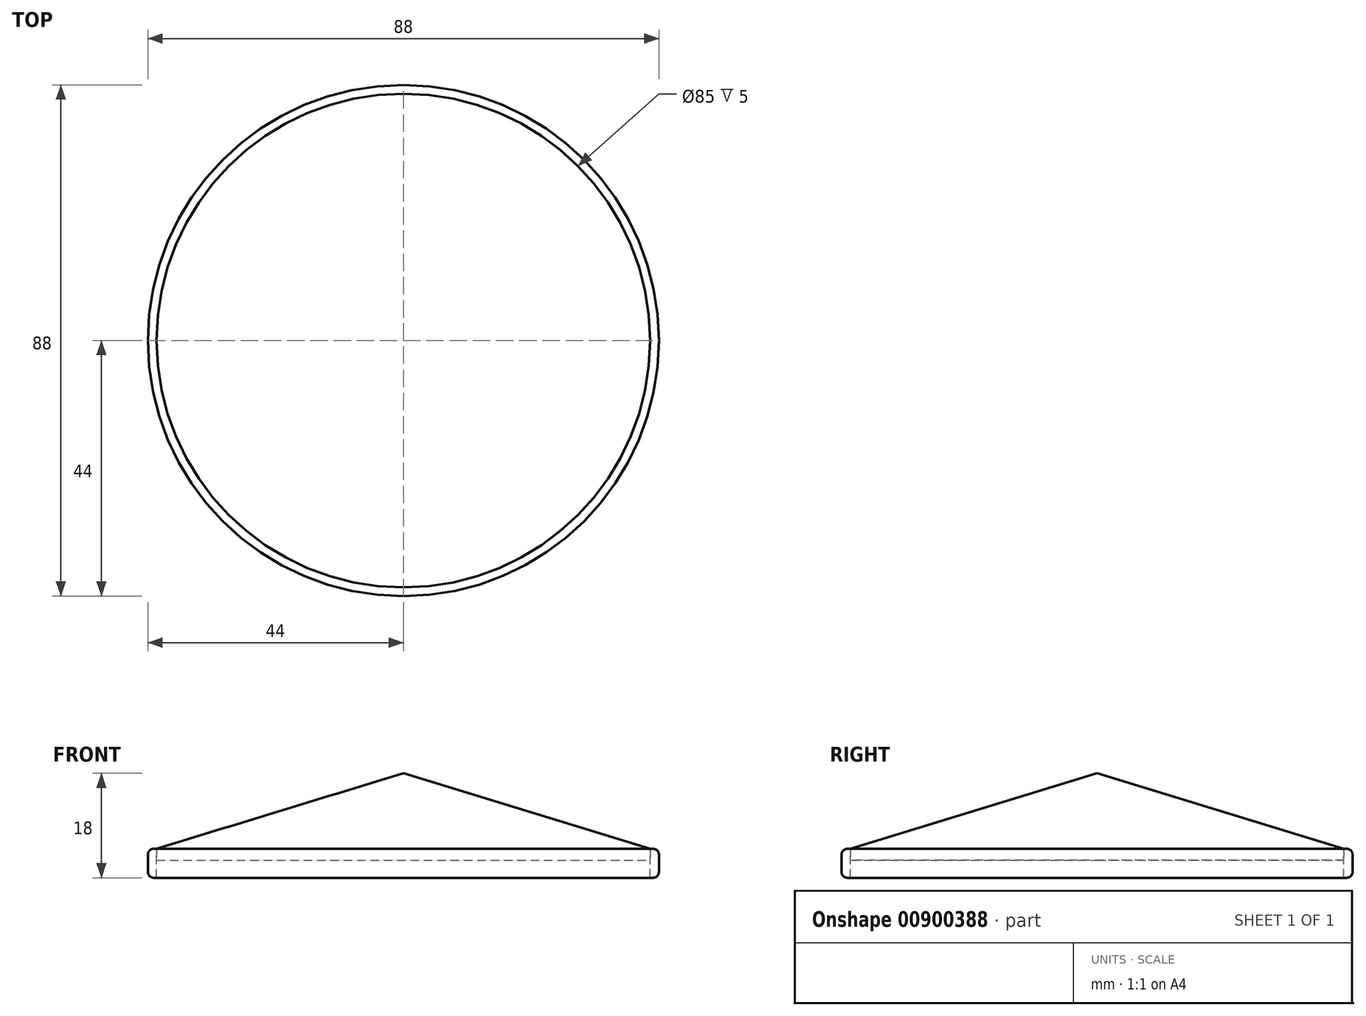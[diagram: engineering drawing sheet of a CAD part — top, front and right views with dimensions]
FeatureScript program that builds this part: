
annotation { "Feature Type Name" : "Feature", "Feature Type Description" : "" }
export const myFeature = defineFeature(function(context is Context, id is Id, definition is map)
    precondition{}
    {
        {
            var Q0;
            Q0=qCreatedBy(makeId("Front.planeOp"),FACE);
            var sketch = newSketch(context, id + "F0", { "sketchPlane" : qUnion([Q0])});
            skLineSegment(sketch, "E0", {"start": v(0, 0) * mm, "end": v(0, 15) * mm});
            skLineSegment(sketch, "E1", {"start": v(42.5, 0) * mm, "end": v(0, 0) * mm});
            skLineSegment(sketch, "E2", {"start": v(42.5, 0) * mm, "end": v(42.5, 2) * mm});
            skLineSegment(sketch, "E3", {"start": v(42.5, 2) * mm, "end": v(0, 15) * mm});
            skSolve(sketch);
        }
        {
            var Q0;
            Q0=makeQuery(id+"F0.imprint","IMPRINT",FACE,{"disambiguationData":[TD([[makeQuery(id+"F0.imprint","IMPRINT",EDGE,{"derivedFrom":sQuery(id+"F0.wireOp",EDGE,"E0")}),-1.0]])]});
            var Q1;
            Q1=sQuery(id+"F0.wireOp",EDGE,"E0");
            revolve(context, id + "F1", {"surfaceOperationType" : NewSurfaceOperationType.NEW, "entities" : qUnion([Q0]), "axis" : qUnion([Q1]), "revolveType" : RevolveType.FULL});
        }
        {
            var Q0;
            Q0=makeQuery(id+"F1.opRevolve","SWEPT_FACE",FACE,{"disambiguationData":[OSD([sQuery(id+"F0.wireOp",EDGE,"E1")])]});
            var sketch = newSketch(context, id + "F2", { "sketchPlane" : qUnion([Q0])});
            skCircle(sketch, "E4", {"center": v(0, 0) * mm, "radius": 44 * mm});
            skSolve(sketch);
        }
        {
            var Q0;
            Q0=makeQuery(id+"F2.imprint","IMPRINT",FACE,{"disambiguationData":[TD([[makeQuery(id+"F2.imprint","IMPRINT",EDGE,{"derivedFrom":sQuery(id+"F2.wireOp",EDGE,"E4")}),1.0]])]});
            extrude(context, id + "F3", {"entities" : qUnion([Q0]), "depth" : 3 * mm, "offsetDistance" : 25 * mm, "hasSecondDirection" : true, "secondDirectionOppositeDirection" : true, "secondDirectionDepth" : 2 * mm});
        }
        {
            var Q0;
            Q0=makeQuery(id+"F3.opExtrude","CAP_EDGE",EDGE,{"disambiguationData":[OSD([sQuery(id+"F2.wireOp",EDGE,"E4")])],"isStart":false});
            var Q1;
            Q1=makeQuery(id+"F3.opExtrude","CAP_EDGE",EDGE,{"disambiguationData":[OSD([sQuery(id+"F2.wireOp",EDGE,"E4")])],"isStart":true});
            fillet(context, id + "F4", {"entities" : qUnion([Q0, Q1]), "radius" : 1 * mm, "tangentPropagation" : true, "allowEdgeOverflow" : false});
        }
    });
